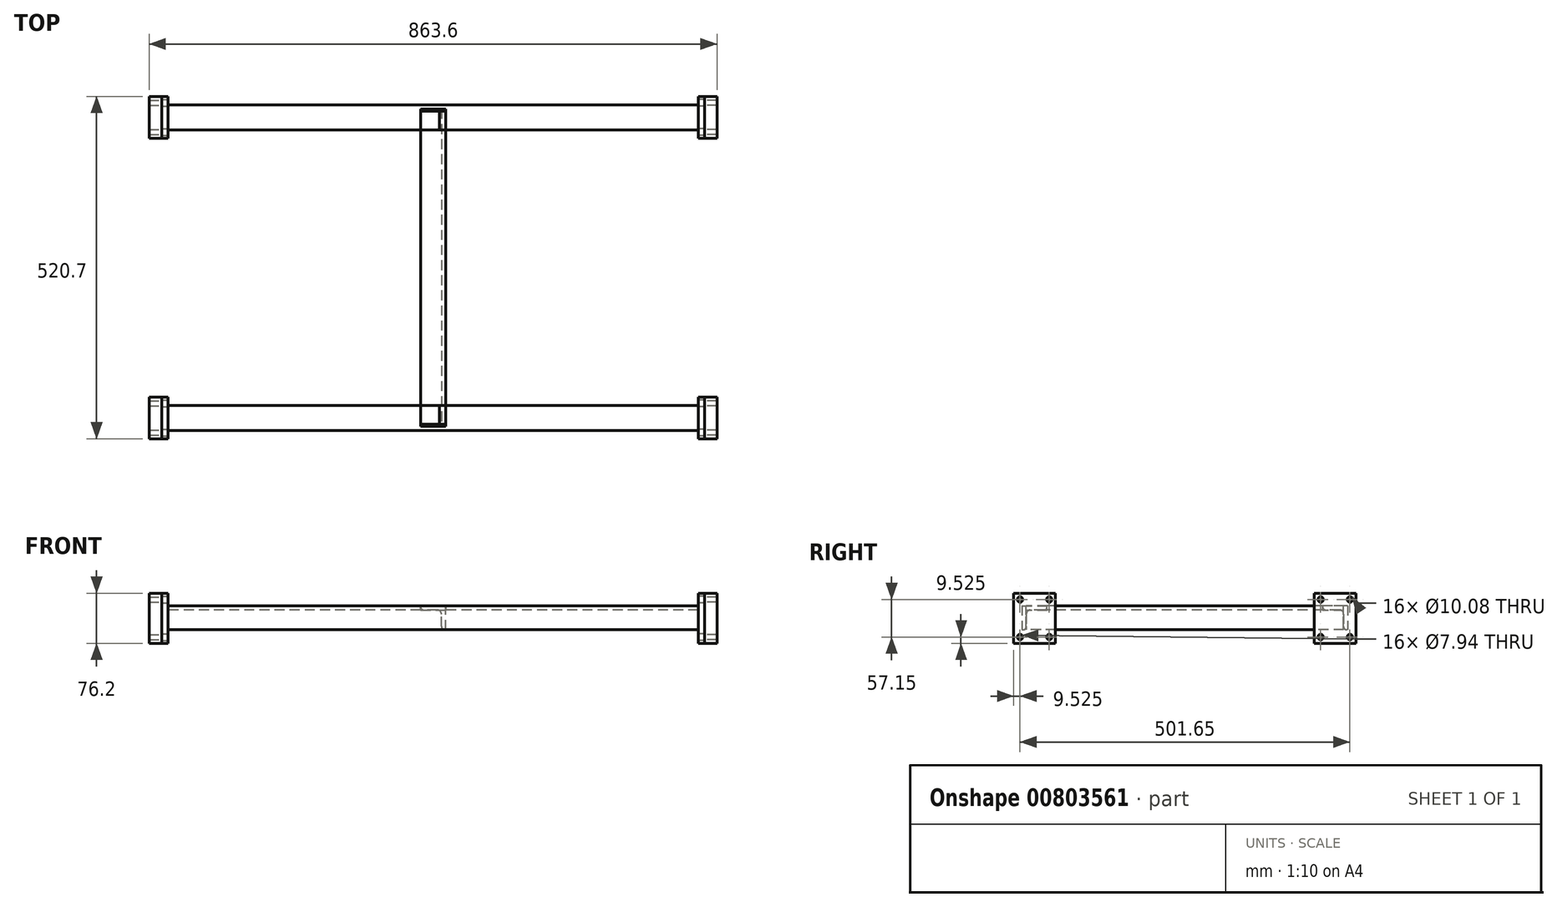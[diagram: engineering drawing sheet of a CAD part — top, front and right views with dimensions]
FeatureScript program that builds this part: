
annotation { "Feature Type Name" : "Feature", "Feature Type Description" : "" }
export const myFeature = defineFeature(function(context is Context, id is Id, definition is map)
    precondition{}
    {
        {
            var Q0;
            Q0=qCreatedBy(makeId("Right.planeOp"),FACE);
            var sketch = newSketch(context, id + "F0", { "sketchPlane" : qUnion([Q0])});
            skLineSegment(sketch, "E0.bottom", {"start": v(-31.75, 38.1) * mm, "end": v(31.75, 38.1) * mm});
            skLineSegment(sketch, "E0.top", {"start": v(-31.75, -38.1) * mm, "end": v(31.75, -38.1) * mm});
            skLineSegment(sketch, "E0.left", {"start": v(-31.75, 38.1) * mm, "end": v(-31.75, -38.1) * mm});
            skLineSegment(sketch, "E0.right", {"start": v(31.75, 38.1) * mm, "end": v(31.75, -38.1) * mm});
            skPoint(sketch, "E0.middle", {"position": v(0, 0) * mm});
            skSolve(sketch);
        }
        {
            var Q0;
            Q0 = qSketchRegion(id + "F0", true);
            extrude(context, id + "F1", {"entities" : qUnion([Q0]), "depth" : 19.05 * mm, "offsetDistance" : 25.4 * mm});
        }
        {
            var Q0;
            Q0=makeQuery(id+"F1.opExtrude","CAP_FACE",FACE,{"disambiguationData":[OSD([sQuery(id+"F0.wireOp",EDGE,"E0.bottom"),sQuery(id+"F0.wireOp",EDGE,"E0.top"),sQuery(id+"F0.wireOp",EDGE,"E0.left"),sQuery(id+"F0.wireOp",EDGE,"E0.right")])],"isStart":true});
            cPlane(context, id + "F2", {"entities" : qUnion([Q0]), "cplaneType" : CPlaneType.OFFSET, "offset" : 431.8 * mm, "oppositeDirection" : true, "width" : 152.4 * mm, "height" : 152.4 * mm});
        }
        {
            var Q0;
            Q0=makeQuery(id+"F1.opExtrude","CAP_FACE",FACE,{"disambiguationData":[OSD([sQuery(id+"F0.wireOp",EDGE,"E0.bottom"),sQuery(id+"F0.wireOp",EDGE,"E0.top"),sQuery(id+"F0.wireOp",EDGE,"E0.left"),sQuery(id+"F0.wireOp",EDGE,"E0.right")])],"isStart":false});
            var sketch = newSketch(context, id + "F3", { "sketchPlane" : qUnion([Q0])});
            skPoint(sketch, "E1.0", {"position": v(0, 0) * mm});
            skLineSegment(sketch, "E2.0.0", {"start": v(-31.75, 38.1) * mm, "end": v(-31.75, -38.1) * mm, "construction": true});
            skLineSegment(sketch, "E2.0.1", {"start": v(-31.75, -38.1) * mm, "end": v(31.75, -38.1) * mm, "construction": true});
            skLineSegment(sketch, "E2.0.2", {"start": v(31.75, -38.1) * mm, "end": v(31.75, 38.1) * mm, "construction": true});
            skLineSegment(sketch, "E2.0.3", {"start": v(31.75, 38.1) * mm, "end": v(-31.75, 38.1) * mm, "construction": true});
            skLineSegment(sketch, "E3.bottom", {"start": v(-22.22, 28.57) * mm, "end": v(22.23, 28.57) * mm, "construction": true});
            skLineSegment(sketch, "E3.top", {"start": v(-22.23, -28.58) * mm, "end": v(22.22, -28.58) * mm, "construction": true});
            skLineSegment(sketch, "E3.left", {"start": v(-22.22, 28.57) * mm, "end": v(-22.23, -28.58) * mm, "construction": true});
            skLineSegment(sketch, "E3.right", {"start": v(22.23, 28.57) * mm, "end": v(22.22, -28.58) * mm, "construction": true});
            skPoint(sketch, "E4", {"position": v(-22.22, 28.57) * mm});
            skPoint(sketch, "E5", {"position": v(22.23, 28.57) * mm});
            skPoint(sketch, "E6", {"position": v(22.22, -28.58) * mm});
            skPoint(sketch, "E7", {"position": v(-22.23, -28.58) * mm});
            skSolve(sketch);
        }
        {
            var Q0;
            Q0=sQuery(id+"F3.wireOp",VERTEX,"E4");
            var Q1;
            Q1=sQuery(id+"F3.wireOp",VERTEX,"E5");
            var Q2;
            Q2=sQuery(id+"F3.wireOp",VERTEX,"E7");
            var Q3;
            Q3=sQuery(id+"F3.wireOp",VERTEX,"E6");
            var Q4;
            Q4=makeQuery(id+"F1.opExtrude","SWEPT_BODY",BODY,{"disambiguationData":[OSD([sQuery(id+"F0.wireOp",EDGE,"E0.bottom"),sQuery(id+"F0.wireOp",EDGE,"E0.top"),sQuery(id+"F0.wireOp",EDGE,"E0.left"),sQuery(id+"F0.wireOp",EDGE,"E0.right")])]});
            hole(context, id + "F4", {"style" : HoleStyle.SIMPLE, "endStyle" : HoleEndStyle.THROUGH, "standardTappedOrClearance" : lookupTablePath({ "standard" : "ANSI", "engagement" : "75%", "pitch" : "16 tpi", "size" : "3/8", "type" : "Tapped" }), "standardBlindInLast" : lookupTablePath({ "standard" : "ANSI", "engagement" : "75%", "pitch" : "16 tpi", "size" : "3/8", "type" : "Tapped" }), "holeDiameter" : 7.94 * mm, "majorDiameter" : 9.52 * mm, "showTappedDepth" : true, "isTappedThrough" : true, "tappedDepth" : 15.24 * mm, "tapClearance" : 3, "locations" : qUnion([Q0, Q1, Q2, Q3]), "scope" : qUnion([Q4])});
        }
        {
            var Q0;
            Q0=makeQuery(id+"F1.opExtrude","SWEPT_BODY",BODY,{"disambiguationData":[OSD([sQuery(id+"F0.wireOp",EDGE,"E0.bottom"),sQuery(id+"F0.wireOp",EDGE,"E0.top"),sQuery(id+"F0.wireOp",EDGE,"E0.left"),sQuery(id+"F0.wireOp",EDGE,"E0.right")])]});
            var Q1;
            Q1=qCreatedBy(id+"F2.planeOp",FACE);
            mirror(context, id + "F5", {"entities" : qUnion([Q0]), "mirrorPlane" : qUnion([Q1])});
        }
        {
            var Q0;
            Q0=qCreatedBy(makeId("Front.planeOp"),FACE);
            cPlane(context, id + "F6", {"entities" : qUnion([Q0]), "cplaneType" : CPlaneType.OFFSET, "offset" : 228.6 * mm, "width" : 152.4 * mm, "height" : 152.4 * mm});
        }
        {
            var Q0;
            Q0=makeQuery(id+"F1.opExtrude","SWEPT_BODY",BODY,{"disambiguationData":[OSD([sQuery(id+"F0.wireOp",EDGE,"E0.bottom"),sQuery(id+"F0.wireOp",EDGE,"E0.top"),sQuery(id+"F0.wireOp",EDGE,"E0.left"),sQuery(id+"F0.wireOp",EDGE,"E0.right")])]});
            var Q1;
            Q1=makeQuery(id+"F5.opPattern","COPY",BODY,{"derivedFrom":makeQuery(id+"F1.opExtrude","SWEPT_BODY",BODY,{"disambiguationData":[OSD([sQuery(id+"F0.wireOp",EDGE,"E0.bottom"),sQuery(id+"F0.wireOp",EDGE,"E0.top"),sQuery(id+"F0.wireOp",EDGE,"E0.left"),sQuery(id+"F0.wireOp",EDGE,"E0.right")])]}),"instanceName":"1"});
            var Q2;
            Q2=qCreatedBy(id+"F6.planeOp",FACE);
            mirror(context, id + "F7", {"entities" : qUnion([Q0, Q1]), "mirrorPlane" : qUnion([Q2])});
        }
        {
            var Q0;
            Q0=makeQuery(id+"F1.opExtrude","CAP_FACE",FACE,{"disambiguationData":[OSD([sQuery(id+"F0.wireOp",EDGE,"E0.bottom"),sQuery(id+"F0.wireOp",EDGE,"E0.top"),sQuery(id+"F0.wireOp",EDGE,"E0.left"),sQuery(id+"F0.wireOp",EDGE,"E0.right")])],"isStart":false});
            var sketch = newSketch(context, id + "F8", { "sketchPlane" : qUnion([Q0])});
            skLineSegment(sketch, "E8.0", {"start": v(-31.75, 38.1) * mm, "end": v(31.75, 38.1) * mm});
            skLineSegment(sketch, "E9.0", {"start": v(31.75, 38.1) * mm, "end": v(31.75, -38.1) * mm});
            skLineSegment(sketch, "E10.0", {"start": v(-31.75, -38.1) * mm, "end": v(31.75, -38.1) * mm});
            skLineSegment(sketch, "E11.0", {"start": v(-31.75, 38.1) * mm, "end": v(-31.75, -38.1) * mm});
            skCircle(sketch, "E12.0", {"center": v(22.23, 28.57) * mm, "radius": 3.97 * mm, "construction": true});
            skCircle(sketch, "E13.0", {"center": v(-22.22, 28.57) * mm, "radius": 3.97 * mm, "construction": true});
            skCircle(sketch, "E14.0", {"center": v(22.22, -28.58) * mm, "radius": 3.97 * mm, "construction": true});
            skCircle(sketch, "E15.0", {"center": v(-22.23, -28.58) * mm, "radius": 3.97 * mm, "construction": true});
            skSolve(sketch);
        }
        {
            var Q0;
            Q0 = qSketchRegion(id + "F8", true);
            extrude(context, id + "F9", {"entities" : qUnion([Q0]), "depth" : 9.52 * mm, "offsetDistance" : 25.4 * mm});
        }
        {
            var Q0;
            Q0=makeQuery(id+"F9.opExtrude","CAP_FACE",FACE,{"disambiguationData":[OSD([sQuery(id+"F8.wireOp",EDGE,"E8.0"),sQuery(id+"F8.wireOp",EDGE,"E9.0"),sQuery(id+"F8.wireOp",EDGE,"E10.0"),sQuery(id+"F8.wireOp",EDGE,"E11.0")])],"isStart":false});
            var sketch = newSketch(context, id + "F10", { "sketchPlane" : qUnion([Q0])});
            skCircle(sketch, "E16.0", {"center": v(-22.22, 28.57) * mm, "radius": 3.97 * mm, "construction": true});
            skCircle(sketch, "E17.0", {"center": v(-22.23, -28.58) * mm, "radius": 3.97 * mm, "construction": true});
            skCircle(sketch, "E18.0", {"center": v(22.22, -28.58) * mm, "radius": 3.97 * mm, "construction": true});
            skCircle(sketch, "E19.0", {"center": v(22.23, 28.57) * mm, "radius": 3.97 * mm, "construction": true});
            skSolve(sketch);
        }
        {
            var Q0;
            Q0=sQuery(id+"F10.wireOp",VERTEX,"E19.0.center");
            var Q1;
            Q1=sQuery(id+"F10.wireOp",VERTEX,"E16.0.center");
            var Q2;
            Q2=sQuery(id+"F10.wireOp",VERTEX,"E18.0.center");
            var Q3;
            Q3=sQuery(id+"F10.wireOp",VERTEX,"E17.0.center");
            var Q4;
            Q4=makeQuery(id+"F9.opExtrude","SWEPT_BODY",BODY,{"disambiguationData":[OSD([sQuery(id+"F8.wireOp",EDGE,"E8.0"),sQuery(id+"F8.wireOp",EDGE,"E9.0"),sQuery(id+"F8.wireOp",EDGE,"E10.0"),sQuery(id+"F8.wireOp",EDGE,"E11.0")])]});
            hole(context, id + "F11", {"style" : HoleStyle.SIMPLE, "endStyle" : HoleEndStyle.THROUGH, "standardTappedOrClearance" : lookupTablePath({ "standard" : "ANSI", "fit" : "Normal (ASME)", "size" : "3/8", "type" : "Clearance" }), "standardBlindInLast" : lookupTablePath({ "fit" : "Free", "standard" : "ANSI", "size" : "3/8", "type" : "Clearance" }), "holeDiameter" : 10.08 * mm, "majorDiameter" : 12.7 * mm, "isTappedThrough" : true, "tappedDepth" : 15.24 * mm, "tapClearance" : 3, "locations" : qUnion([Q0, Q1, Q2, Q3]), "scope" : qUnion([Q4])});
        }
        {
            var Q0;
            Q0=makeQuery(id+"F9.opExtrude","SWEPT_BODY",BODY,{"disambiguationData":[OSD([sQuery(id+"F8.wireOp",EDGE,"E8.0"),sQuery(id+"F8.wireOp",EDGE,"E9.0"),sQuery(id+"F8.wireOp",EDGE,"E10.0"),sQuery(id+"F8.wireOp",EDGE,"E11.0")])]});
            var Q1;
            Q1=qCreatedBy(id+"F2.planeOp",FACE);
            mirror(context, id + "F12", {"entities" : qUnion([Q0]), "mirrorPlane" : qUnion([Q1])});
        }
        {
            var Q0;
            Q0=makeQuery(id+"F9.opExtrude","SWEPT_BODY",BODY,{"disambiguationData":[OSD([sQuery(id+"F8.wireOp",EDGE,"E8.0"),sQuery(id+"F8.wireOp",EDGE,"E9.0"),sQuery(id+"F8.wireOp",EDGE,"E10.0"),sQuery(id+"F8.wireOp",EDGE,"E11.0")])]});
            var Q1;
            Q1=makeQuery(id+"F12.opPattern","COPY",BODY,{"derivedFrom":makeQuery(id+"F9.opExtrude","SWEPT_BODY",BODY,{"disambiguationData":[OSD([sQuery(id+"F8.wireOp",EDGE,"E8.0"),sQuery(id+"F8.wireOp",EDGE,"E9.0"),sQuery(id+"F8.wireOp",EDGE,"E10.0"),sQuery(id+"F8.wireOp",EDGE,"E11.0")])]}),"instanceName":"1"});
            var Q2;
            Q2=qCreatedBy(id+"F6.planeOp",FACE);
            mirror(context, id + "F13", {"entities" : qUnion([Q0, Q1]), "mirrorPlane" : qUnion([Q2])});
        }
        {
            var Q0;
            Q0=makeQuery(id+"F13.opPattern","COPY",FACE,{"derivedFrom":makeQuery(id+"F9.opExtrude","CAP_FACE",FACE,{"disambiguationData":[OSD([sQuery(id+"F8.wireOp",EDGE,"E8.0"),sQuery(id+"F8.wireOp",EDGE,"E9.0"),sQuery(id+"F8.wireOp",EDGE,"E10.0"),sQuery(id+"F8.wireOp",EDGE,"E11.0")])],"isStart":false}),"instanceName":"1"});
            var sketch = newSketch(context, id + "F14", { "sketchPlane" : qUnion([Q0])});
            skLineSegment(sketch, "E20.0", {"start": v(-425.45, 38.1) * mm, "end": v(-488.95, 38.1) * mm, "construction": true});
            skLineSegment(sketch, "E21.0", {"start": v(-425.45, 38.1) * mm, "end": v(-425.45, -38.1) * mm, "construction": true});
            skLineSegment(sketch, "E22.0", {"start": v(-425.45, -38.1) * mm, "end": v(-488.95, -38.1) * mm, "construction": true});
            skLineSegment(sketch, "E23.0", {"start": v(-488.95, 38.1) * mm, "end": v(-488.95, -38.1) * mm, "construction": true});
            skLineSegment(sketch, "E24", {"start": v(-457.2, 38.1) * mm, "end": v(-457.2, -38.1) * mm, "construction": true});
            skLineSegment(sketch, "E25", {"start": v(-425.45, 0) * mm, "end": v(-488.95, 0) * mm, "construction": true});
            skLineSegment(sketch, "E26.bottom", {"start": v(-476.25, 19.05) * mm, "end": v(-438.15, 19.05) * mm});
            skLineSegment(sketch, "E26.top", {"start": v(-476.25, -17.46) * mm, "end": v(-474.66, -17.46) * mm});
            skLineSegment(sketch, "E26.left", {"start": v(-476.25, 19.05) * mm, "end": v(-476.25, -17.46) * mm});
            skLineSegment(sketch, "E26.right", {"start": v(-438.15, 19.05) * mm, "end": v(-438.15, 17.46) * mm});
            skLineSegment(sketch, "E27.0", {"start": v(-463.55, 12.7) * mm, "end": v(-442.91, 12.7) * mm});
            skLineSegment(sketch, "E28.0", {"start": v(-469.9, 6.35) * mm, "end": v(-469.9, -12.7) * mm});
            skArc(sketch, "E29.filletArc", {"start": v(-463.55, 12.7) * mm, "mid": v(-468.04, 10.84) * mm, "end": v(-469.9, 6.35) * mm});
            skPoint(sketch, "E30.newPointB", {"position": v(-438.15, -19.05) * mm});
            skArc(sketch, "E30.filletArc", {"start": v(-442.91, 12.7) * mm, "mid": v(-439.54, 14.1) * mm, "end": v(-438.15, 17.46) * mm});
            skArc(sketch, "E31.filletArc", {"start": v(-474.66, -17.46) * mm, "mid": v(-471.3, -16.07) * mm, "end": v(-469.9, -12.7) * mm});
            skSolve(sketch);
        }
        {
            var Q0;
            Q0 = qSketchRegion(id + "F14", true);
            extrude(context, id + "F15", {"entities" : qUnion([Q0]), "depth" : 806.45 * mm, "offsetDistance" : 25.4 * mm});
        }
        {
            var Q0;
            Q0=makeQuery(id+"F15.opExtrude","SWEPT_BODY",BODY,{"disambiguationData":[OSD([sQuery(id+"F14.wireOp",EDGE,"E26.bottom"),sQuery(id+"F14.wireOp",EDGE,"E26.top"),sQuery(id+"F14.wireOp",EDGE,"E26.left"),sQuery(id+"F14.wireOp",EDGE,"E26.right"),sQuery(id+"F14.wireOp",EDGE,"E27.0"),sQuery(id+"F14.wireOp",EDGE,"E28.0"),sQuery(id+"F14.wireOp",EDGE,"E29.filletArc"),sQuery(id+"F14.wireOp",EDGE,"E30.filletArc"),sQuery(id+"F14.wireOp",EDGE,"E31.filletArc")])]});
            var Q1;
            Q1=qCreatedBy(id+"F6.planeOp",FACE);
            mirror(context, id + "F16", {"entities" : qUnion([Q0]), "mirrorPlane" : qUnion([Q1])});
        }
        {
            var Q0;
            Q0=makeQuery(id+"F15.opExtrude","SWEPT_FACE",FACE,{"disambiguationData":[OSD([sQuery(id+"F14.wireOp",EDGE,"E26.left")])]});
            cPlane(context, id + "F17", {"entities" : qUnion([Q0]), "cplaneType" : CPlaneType.OFFSET, "offset" : 6.35 * mm, "oppositeDirection" : true, "width" : 152.4 * mm, "height" : 152.4 * mm});
        }
        {
            var Q0;
            Q0=qCreatedBy(id+"F17.planeOp",FACE);
            var sketch = newSketch(context, id + "F18", { "sketchPlane" : qUnion([Q0])});
            skLineSegment(sketch, "E32.0", {"start": v(835.03, -17.46) * mm, "end": v(28.58, -17.46) * mm, "construction": true});
            skLineSegment(sketch, "E33", {"start": v(431.8, -17.46) * mm, "end": v(431.8, 108.32) * mm, "construction": true});
            skLineSegment(sketch, "E34.bottom", {"start": v(450.85, -17.46) * mm, "end": v(449.58, -17.46) * mm});
            skLineSegment(sketch, "E34.top", {"start": v(450.85, 19.05) * mm, "end": v(412.75, 19.05) * mm});
            skLineSegment(sketch, "E34.left", {"start": v(450.85, -17.46) * mm, "end": v(450.85, 19.05) * mm});
            skLineSegment(sketch, "E34.right", {"start": v(412.75, 17.78) * mm, "end": v(412.75, 19.05) * mm});
            skLineSegment(sketch, "E35.0", {"start": v(438.15, 12.7) * mm, "end": v(417.83, 12.7) * mm});
            skLineSegment(sketch, "E36.0", {"start": v(444.5, -12.38) * mm, "end": v(444.5, 6.35) * mm});
            skArc(sketch, "E37.filletArc", {"start": v(444.5, 6.35) * mm, "mid": v(442.64, 10.84) * mm, "end": v(438.15, 12.7) * mm});
            skArc(sketch, "E38.filletArc", {"start": v(412.75, 17.78) * mm, "mid": v(414.24, 14.19) * mm, "end": v(417.83, 12.7) * mm});
            skArc(sketch, "E39.filletArc", {"start": v(444.5, -12.38) * mm, "mid": v(445.99, -15.97) * mm, "end": v(449.58, -17.46) * mm});
            skLineSegment(sketch, "E40.0", {"start": v(835.03, 19.05) * mm, "end": v(28.58, 19.05) * mm, "construction": true});
            skSolve(sketch);
        }
        {
            var Q0;
            Q0 = qSketchRegion(id + "F18", true);
            extrude(context, id + "F19", {"entities" : qUnion([Q0]), "oppositeDirection" : true, "depth" : 482.6 * mm, "offsetDistance" : 25.4 * mm});
        }
        {
            var Q0;
            Q0=makeQuery(id+"F19.opExtrude","SWEPT_FACE",FACE,{"disambiguationData":[OSD([sQuery(id+"F18.wireOp",EDGE,"E34.top")])]});
            var sketch = newSketch(context, id + "F20", { "sketchPlane" : qUnion([Q0])});
            skLineSegment(sketch, "E41", {"start": v(450.85, -228.6) * mm, "end": v(341.5, -228.6) * mm, "construction": true});
            skLineSegment(sketch, "E42.bottom", {"start": v(450.85, -469.9) * mm, "end": v(412.75, -469.9) * mm});
            skLineSegment(sketch, "E42.top", {"start": v(450.85, -438.15) * mm, "end": v(412.75, -438.15) * mm});
            skLineSegment(sketch, "E42.left", {"start": v(450.85, -469.9) * mm, "end": v(450.85, -438.15) * mm});
            skLineSegment(sketch, "E42.right", {"start": v(412.75, -469.9) * mm, "end": v(412.75, -438.15) * mm});
            skLineSegment(sketch, "E43.MirrorCS", {"start": v(412.75, 12.7) * mm, "end": v(412.75, -19.05) * mm});
            skLineSegment(sketch, "E44.MirrorCS", {"start": v(450.85, 12.7) * mm, "end": v(450.85, -19.05) * mm});
            skLineSegment(sketch, "E45.MirrorCS", {"start": v(450.85, -19.05) * mm, "end": v(412.75, -19.05) * mm});
            skLineSegment(sketch, "E46.MirrorCS", {"start": v(450.85, 12.7) * mm, "end": v(412.75, 12.7) * mm});
            skSolve(sketch);
        }
        {
            var Q0;
            Q0 = qSketchRegion(id + "F20", true);
            extrude(context, id + "F21", {"entities" : qUnion([Q0]), "operationType" : NewBodyOperationType.REMOVE, "oppositeDirection" : true, "depth" : 7.11 * mm, "offsetDistance" : 25.4 * mm});
        }
        {
            var Q0;
            Q0=makeQuery(id+"F19.opExtrude","SWEPT_FACE",FACE,{"disambiguationData":[OSD([sQuery(id+"F18.wireOp",EDGE,"E34.top")])]});
            var sketch = newSketch(context, id + "F22", { "sketchPlane" : qUnion([Q0])});
            skLineSegment(sketch, "E47.0", {"start": v(835.03, -476.25) * mm, "end": v(28.58, -476.25) * mm, "construction": true});
            skLineSegment(sketch, "E48.0", {"start": v(835.03, 19.05) * mm, "end": v(28.58, 19.05) * mm, "construction": true});
            skLineSegment(sketch, "E49", {"start": v(431.8, -476.25) * mm, "end": v(431.8, 19.05) * mm, "construction": true});
            skLineSegment(sketch, "E50", {"start": v(431.8, -228.6) * mm, "end": v(650.48, -228.6) * mm, "construction": true});
            skLineSegment(sketch, "E51.0", {"start": v(431.8, -457.2) * mm, "end": v(650.48, -457.2) * mm, "construction": true});
            skPoint(sketch, "E52", {"position": v(431.8, -457.2) * mm});
            skPoint(sketch, "E53.MirrorP", {"position": v(431.8, 0) * mm});
            skSolve(sketch);
        }
        {
            var Q0;
            Q0=sQuery(id+"F22.wireOp",VERTEX,"E52");
            var Q1;
            Q1=sQuery(id+"F22.wireOp",VERTEX,"E53.MirrorP");
            var Q2;
            Q2=makeQuery(id+"F15.opExtrude","SWEPT_BODY",BODY,{"disambiguationData":[OSD([sQuery(id+"F14.wireOp",EDGE,"E26.bottom"),sQuery(id+"F14.wireOp",EDGE,"E26.top"),sQuery(id+"F14.wireOp",EDGE,"E26.left"),sQuery(id+"F14.wireOp",EDGE,"E26.right"),sQuery(id+"F14.wireOp",EDGE,"E27.0"),sQuery(id+"F14.wireOp",EDGE,"E28.0"),sQuery(id+"F14.wireOp",EDGE,"E29.filletArc"),sQuery(id+"F14.wireOp",EDGE,"E30.filletArc"),sQuery(id+"F14.wireOp",EDGE,"E31.filletArc")])]});
            var Q3;
            Q3=makeQuery(id+"F16.opPattern","COPY",BODY,{"derivedFrom":makeQuery(id+"F15.opExtrude","SWEPT_BODY",BODY,{"disambiguationData":[OSD([sQuery(id+"F14.wireOp",EDGE,"E26.bottom"),sQuery(id+"F14.wireOp",EDGE,"E26.top"),sQuery(id+"F14.wireOp",EDGE,"E26.left"),sQuery(id+"F14.wireOp",EDGE,"E26.right"),sQuery(id+"F14.wireOp",EDGE,"E27.0"),sQuery(id+"F14.wireOp",EDGE,"E28.0"),sQuery(id+"F14.wireOp",EDGE,"E29.filletArc"),sQuery(id+"F14.wireOp",EDGE,"E30.filletArc"),sQuery(id+"F14.wireOp",EDGE,"E31.filletArc")])]}),"instanceName":"1"});
            hole(context, id + "F23", {"style" : HoleStyle.SIMPLE, "endStyle" : HoleEndStyle.THROUGH, "standardTappedOrClearance" : lookupTablePath({ "standard" : "ANSI", "size" : "5/8 (0.62)", "type" : "Drilled" }), "standardBlindInLast" : lookupTablePath({ "standard" : "ANSI", "size" : "5/8", "type" : "Drilled" }), "holeDiameter" : 5 / 203.2 * mm, "majorDiameter" : 9.52 * mm, "isTappedThrough" : true, "tappedDepth" : 15.24 * mm, "tapClearance" : 3, "locations" : qUnion([Q0, Q1]), "scope" : qUnion([Q2, Q3])});
        }
    });
